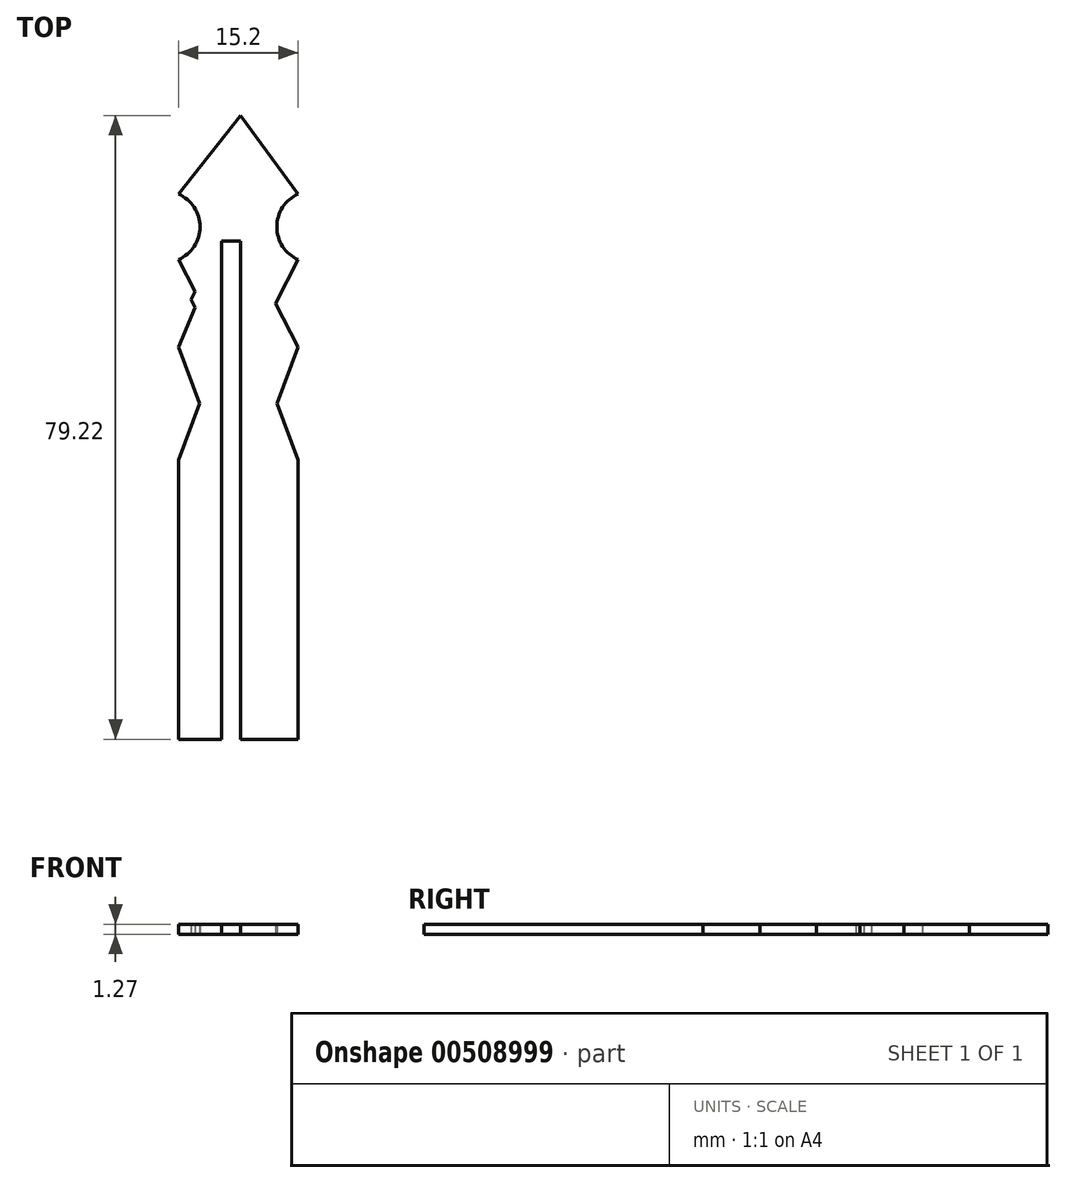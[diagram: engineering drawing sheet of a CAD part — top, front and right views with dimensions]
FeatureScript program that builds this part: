
annotation { "Feature Type Name" : "Feature", "Feature Type Description" : "" }
export const myFeature = defineFeature(function(context is Context, id is Id, definition is map)
    precondition{}
    {
        {
            var Q0;
            Q0=qCreatedBy(makeId("Top.planeOp"),FACE);
            var sketch = newSketch(context, id + "F0", { "sketchPlane" : qUnion([Q0])});
            skLineSegment(sketch, "E0.top", {"start": v(-7.9, -9.46) * mm, "end": v(7.3, -9.46) * mm});
            skLineSegment(sketch, "E1.bottom", {"start": v(-2.44, 28.45) * mm, "end": v(0, 28.45) * mm});
            skLineSegment(sketch, "E1.top", {"start": v(-2.44, -9.46) * mm, "end": v(0, -9.46) * mm});
            skLineSegment(sketch, "E1.left", {"start": v(-2.44, 28.45) * mm, "end": v(-2.44, -9.46) * mm});
            skLineSegment(sketch, "E1.right", {"start": v(0, 28.45) * mm, "end": v(0, -9.46) * mm});
            skLineSegment(sketch, "E2", {"start": v(-7.9, 34.4) * mm, "end": v(0, 44.36) * mm});
            skPoint(sketch, "E2.endSnap0", {"position": v(-0.3, 44.36) * mm});
            skLineSegment(sketch, "E3", {"start": v(0, 44.36) * mm, "end": v(7.3, 34.4) * mm});
            skLineSegment(sketch, "E4", {"start": v(-7.9, 34.4) * mm, "end": v(7.3, 34.4) * mm});
            skArc(sketch, "E5", {"start": v(7.3, 34.4) * mm, "mid": v(4.6, 30.24) * mm, "end": v(7.3, 26.06) * mm});
            skArc(sketch, "E6", {"start": v(-7.9, 26.06) * mm, "mid": v(-5.16, 30.24) * mm, "end": v(-7.9, 34.4) * mm});
            skLineSegment(sketch, "E7", {"start": v(7.3, 26.06) * mm, "end": v(4.41, 20.5) * mm});
            skLineSegment(sketch, "E8", {"start": v(4.41, 20.5) * mm, "end": v(7.3, 14.95) * mm});
            skLineSegment(sketch, "E9", {"start": v(-5.77, 22) * mm, "end": v(-6.29, 21) * mm});
            skLineSegment(sketch, "E10", {"start": v(-6.29, 21) * mm, "end": v(-5.77, 19.99) * mm});
            skLineSegment(sketch, "E11", {"start": v(-5.77, 22) * mm, "end": v(-7.9, 26.06) * mm});
            skLineSegment(sketch, "E12", {"start": v(-5.77, 19.99) * mm, "end": v(-7.9, 14.95) * mm});
            skLineSegment(sketch, "E13", {"start": v(5.18, 22) * mm, "end": v(5.8, 21) * mm});
            skLineSegment(sketch, "E14", {"start": v(5.8, 21) * mm, "end": v(4.68, 19.99) * mm});
            skLineSegment(sketch, "E15", {"start": v(7.3, 14.95) * mm, "end": v(4.63, 7.79) * mm});
            skLineSegment(sketch, "E16", {"start": v(4.63, 7.79) * mm, "end": v(7.3, 0.6) * mm});
            skLineSegment(sketch, "E17", {"start": v(-7.9, 14.95) * mm, "end": v(-5.23, 7.79) * mm});
            skLineSegment(sketch, "E18", {"start": v(-5.23, 7.79) * mm, "end": v(-7.9, 0.6) * mm});
            skLineSegment(sketch, "E19", {"start": v(-7.9, 0.6) * mm, "end": v(-7.9, -9.46) * mm});
            skLineSegment(sketch, "E20", {"start": v(7.3, 0.6) * mm, "end": v(7.3, -9.46) * mm});
            skSolve(sketch);
        }
        {
            var Q0;
            Q0=makeQuery(id+"F0.imprint","IMPRINT",FACE,{"disambiguationData":[TD([[makeQuery(id+"F0.imprint","IMPRINT",EDGE,{"derivedFrom":sQuery(id+"F0.wireOp",EDGE,"E1.bottom")}),1.0]])]});
            var Q1;
            Q1=makeQuery(id+"F0.imprint","IMPRINT",FACE,{"disambiguationData":[TD([[makeQuery(id+"F0.imprint","IMPRINT",EDGE,{"derivedFrom":sQuery(id+"F0.wireOp",EDGE,"E2")}),-1.0]])]});
            extrude(context, id + "F1", {"entities" : qUnion([Q0, Q1]), "depth" : 1.27 * mm});
        }
        {
            var Q0;
            {var subQ0=sQuery(id+"F0.wireOp",EDGE,"E0.top");Q0=makeQuery(id+"F1.opExtrude","SWEPT_FACE",FACE,{"disambiguationData":[OSD([subQ0]),TDD([makeQuery(id+"F0.imprint","IMPRINT",EDGE,{"disambiguationData":[TD([[makeQuery(id+"F0.imprint","INTERSECT",VERTEX,{"derivedFrom":[subQ0,sQuery(id+"F0.wireOp",EDGE,"E19")]}),-1.0]])],"derivedFrom":subQ0})])]});}
            var Q1;
            {var subQ0=sQuery(id+"F0.wireOp",EDGE,"E0.top");Q1=makeQuery(id+"F1.opExtrude","SWEPT_FACE",FACE,{"disambiguationData":[OSD([subQ0]),TDD([makeQuery(id+"F0.imprint","IMPRINT",EDGE,{"disambiguationData":[TD([[makeQuery(id+"F0.imprint","INTERSECT",VERTEX,{"derivedFrom":[subQ0,sQuery(id+"F0.wireOp",EDGE,"E20")]}),1.0]])],"derivedFrom":subQ0})])]});}
            extrude(context, id + "F2", {"entities" : qUnion([Q0, Q1]), "operationType" : NewBodyOperationType.ADD, "depth" : 25.4 * mm});
        }
    });
